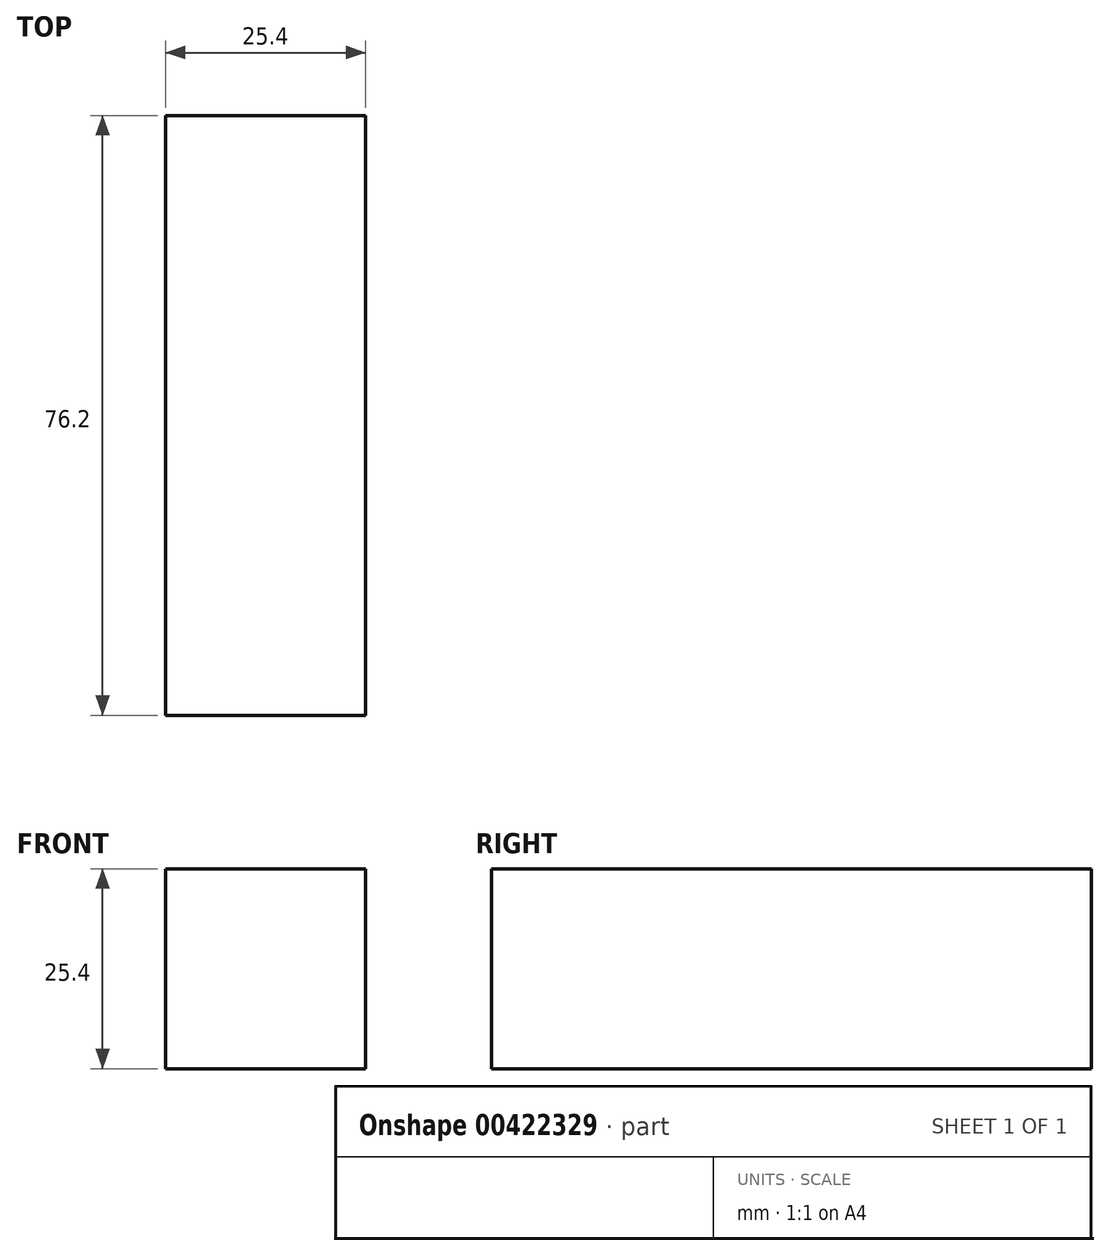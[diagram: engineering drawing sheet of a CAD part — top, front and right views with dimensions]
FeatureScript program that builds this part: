
annotation { "Feature Type Name" : "Feature", "Feature Type Description" : "" }
export const myFeature = defineFeature(function(context is Context, id is Id, definition is map)
    precondition{}
    {
        {
            var Q0;
            Q0=qCreatedBy(makeId("Front.planeOp"),FACE);
            var sketch = newSketch(context, id + "F0", { "sketchPlane" : qUnion([Q0])});
            skLineSegment(sketch, "E0.bottom", {"start": v(-15.33, 17.68) * mm, "end": v(10.07, 17.68) * mm});
            skLineSegment(sketch, "E0.top", {"start": v(-15.33, -7.72) * mm, "end": v(10.07, -7.72) * mm});
            skLineSegment(sketch, "E0.left", {"start": v(-15.33, 17.68) * mm, "end": v(-15.33, -7.72) * mm});
            skLineSegment(sketch, "E0.right", {"start": v(10.07, 17.68) * mm, "end": v(10.07, -7.72) * mm});
            skSolve(sketch);
        }
        {
            var Q0;
            Q0 = qSketchRegion(id + "F0", true);
            extrude(context, id + "F1", {"entities" : qUnion([Q0]), "depth" : 76.2 * mm});
        }
    });
